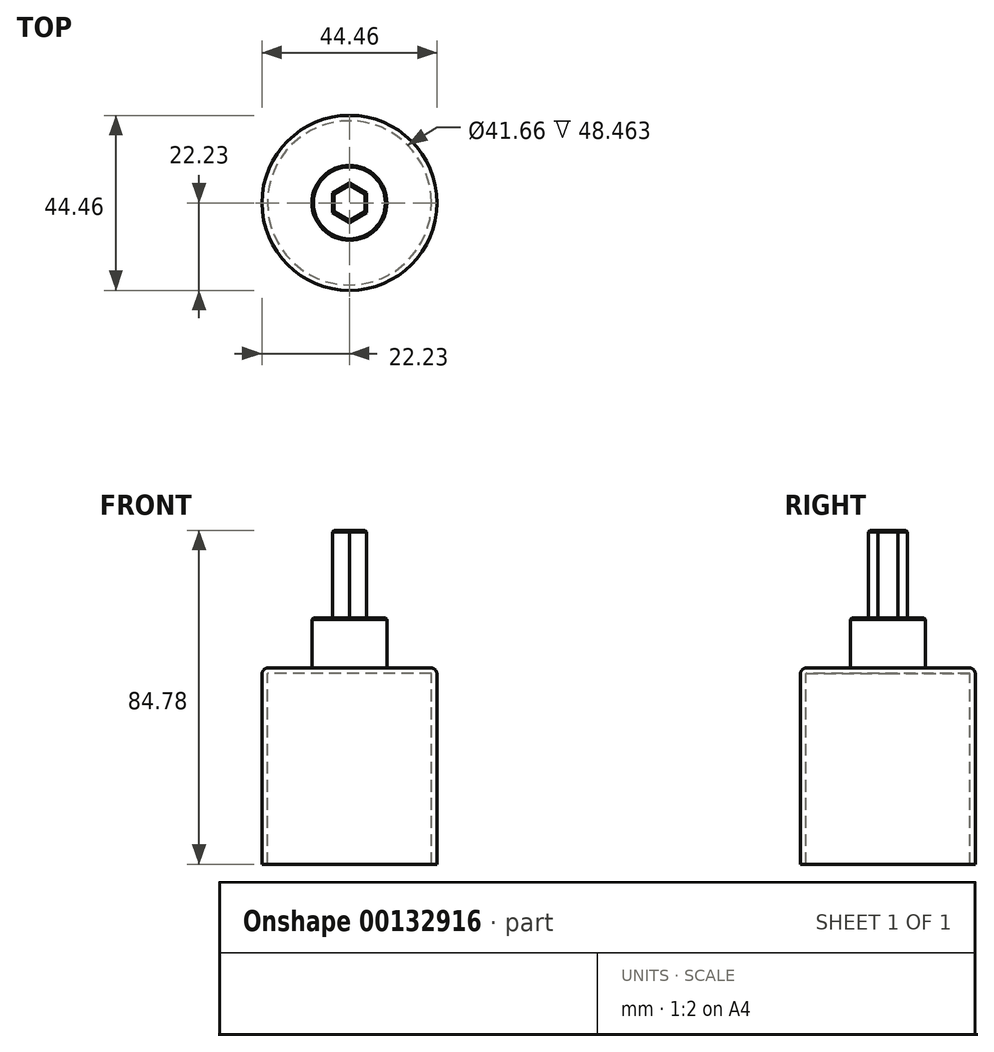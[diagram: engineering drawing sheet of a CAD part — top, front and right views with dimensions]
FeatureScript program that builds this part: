
annotation { "Feature Type Name" : "Feature", "Feature Type Description" : "" }
export const myFeature = defineFeature(function(context is Context, id is Id, definition is map)
    precondition{}
    {
        {
            var Q0;
            Q0=qCreatedBy(makeId("Top.planeOp"),FACE);
            var sketch = newSketch(context, id + "F0", { "sketchPlane" : qUnion([Q0])});
            skCircle(sketch, "E0", {"center": v(0, 0) * mm, "radius": 22.23 * mm});
            skCircle(sketch, "E1", {"center": v(0, 0) * mm, "radius": 9.53 * mm});
            skCircle(sketch, "E2.cCircle", {"center": v(0, 0) * mm, "radius": 4.32 * mm, "construction": true});
            skLineSegment(sketch, "E2.0", {"start": v(0, 4.99) * mm, "end": v(4.32, 2.5) * mm});
            skLineSegment(sketch, "E2.1", {"start": v(4.32, 2.5) * mm, "end": v(4.32, -2.5) * mm});
            skLineSegment(sketch, "E2.2", {"start": v(4.32, -2.5) * mm, "end": v(0, -4.99) * mm});
            skLineSegment(sketch, "E2.3", {"start": v(0, -4.99) * mm, "end": v(-4.32, -2.5) * mm});
            skLineSegment(sketch, "E2.4", {"start": v(-4.32, -2.5) * mm, "end": v(-4.32, 2.5) * mm});
            skLineSegment(sketch, "E2.5", {"start": v(-4.32, 2.5) * mm, "end": v(0, 4.99) * mm});
            skPoint(sketch, "E2.0.midPoint", {"position": v(2.16, 3.74) * mm});
            skSolve(sketch);
        }
        {
            var Q0;
            Q0=makeQuery(id+"F0.imprint","IMPRINT",FACE,{"disambiguationData":[TD([[makeQuery(id+"F0.imprint","IMPRINT",EDGE,{"derivedFrom":sQuery(id+"F0.wireOp",EDGE,"E0")}),1.0]])]});
            var Q1;
            Q1=makeQuery(id+"F0.imprint","IMPRINT",FACE,{"disambiguationData":[TD([[makeQuery(id+"F0.imprint","IMPRINT",EDGE,{"derivedFrom":sQuery(id+"F0.wireOp",EDGE,"E1")}),1.0]])]});
            var Q2;
            Q2=makeQuery(id+"F0.imprint","IMPRINT",FACE,{"disambiguationData":[TD([[makeQuery(id+"F0.imprint","IMPRINT",EDGE,{"derivedFrom":sQuery(id+"F0.wireOp",EDGE,"E2.0")}),-1.0]])]});
            extrude(context, id + "F1", {"entities" : qUnion([Q0, Q1, Q2]), "oppositeDirection" : true, "depth" : 49.86 * mm});
        }
        {
            var Q0;
            Q0=makeQuery(id+"F1.opExtrude","CAP_FACE",FACE,{"disambiguationData":[OSD([sQuery(id+"F0.wireOp",EDGE,"E0")])],"isStart":false});
            shell(context, id + "F2", {"entities" : qUnion([Q0]), "thickness" : 1.4 * mm});
        }
        {
            var Q0;
            Q0=makeQuery(id+"F1.opExtrude","CAP_EDGE",EDGE,{"disambiguationData":[OSD([sQuery(id+"F0.wireOp",EDGE,"E0")])],"isStart":true});
            fillet(context, id + "F3", {"entities" : qUnion([Q0]), "radius" : 1.59 * mm, "tangentPropagation" : true, "allowEdgeOverflow" : false});
        }
        {
            var Q0;
            Q0=makeQuery(id+"F0.imprint","IMPRINT",FACE,{"disambiguationData":[TD([[makeQuery(id+"F0.imprint","IMPRINT",EDGE,{"derivedFrom":sQuery(id+"F0.wireOp",EDGE,"E2.0")}),-1.0]])]});
            extrude(context, id + "F4", {"entities" : qUnion([Q0]), "operationType" : NewBodyOperationType.ADD, "depth" : 34.92 * mm});
        }
        {
            var Q0;
            Q0=makeQuery(id+"F0.imprint","IMPRINT",FACE,{"disambiguationData":[TD([[makeQuery(id+"F0.imprint","IMPRINT",EDGE,{"derivedFrom":sQuery(id+"F0.wireOp",EDGE,"E1")}),1.0]])]});
            extrude(context, id + "F5", {"entities" : qUnion([Q0]), "operationType" : NewBodyOperationType.ADD, "depth" : 12.7 * mm});
        }
        {
            var Q0;
            Q0=makeQuery(id+"F4.opExtrude","CAP_FACE",FACE,{"disambiguationData":[OSD([sQuery(id+"F0.wireOp",EDGE,"E2.0"),sQuery(id+"F0.wireOp",EDGE,"E2.1"),sQuery(id+"F0.wireOp",EDGE,"E2.2"),sQuery(id+"F0.wireOp",EDGE,"E2.3"),sQuery(id+"F0.wireOp",EDGE,"E2.4"),sQuery(id+"F0.wireOp",EDGE,"E2.5")])],"isStart":false});
            var Q1;
            Q1=makeQuery(id+"F5.opExtrude","CAP_EDGE",EDGE,{"disambiguationData":[OSD([sQuery(id+"F0.wireOp",EDGE,"E1")])],"isStart":false});
            chamfer(context, id + "F6", {"entities" : qUnion([Q0, Q1]), "width" : 0.38 * mm, "tangentPropagation" : true});
        }
    });
